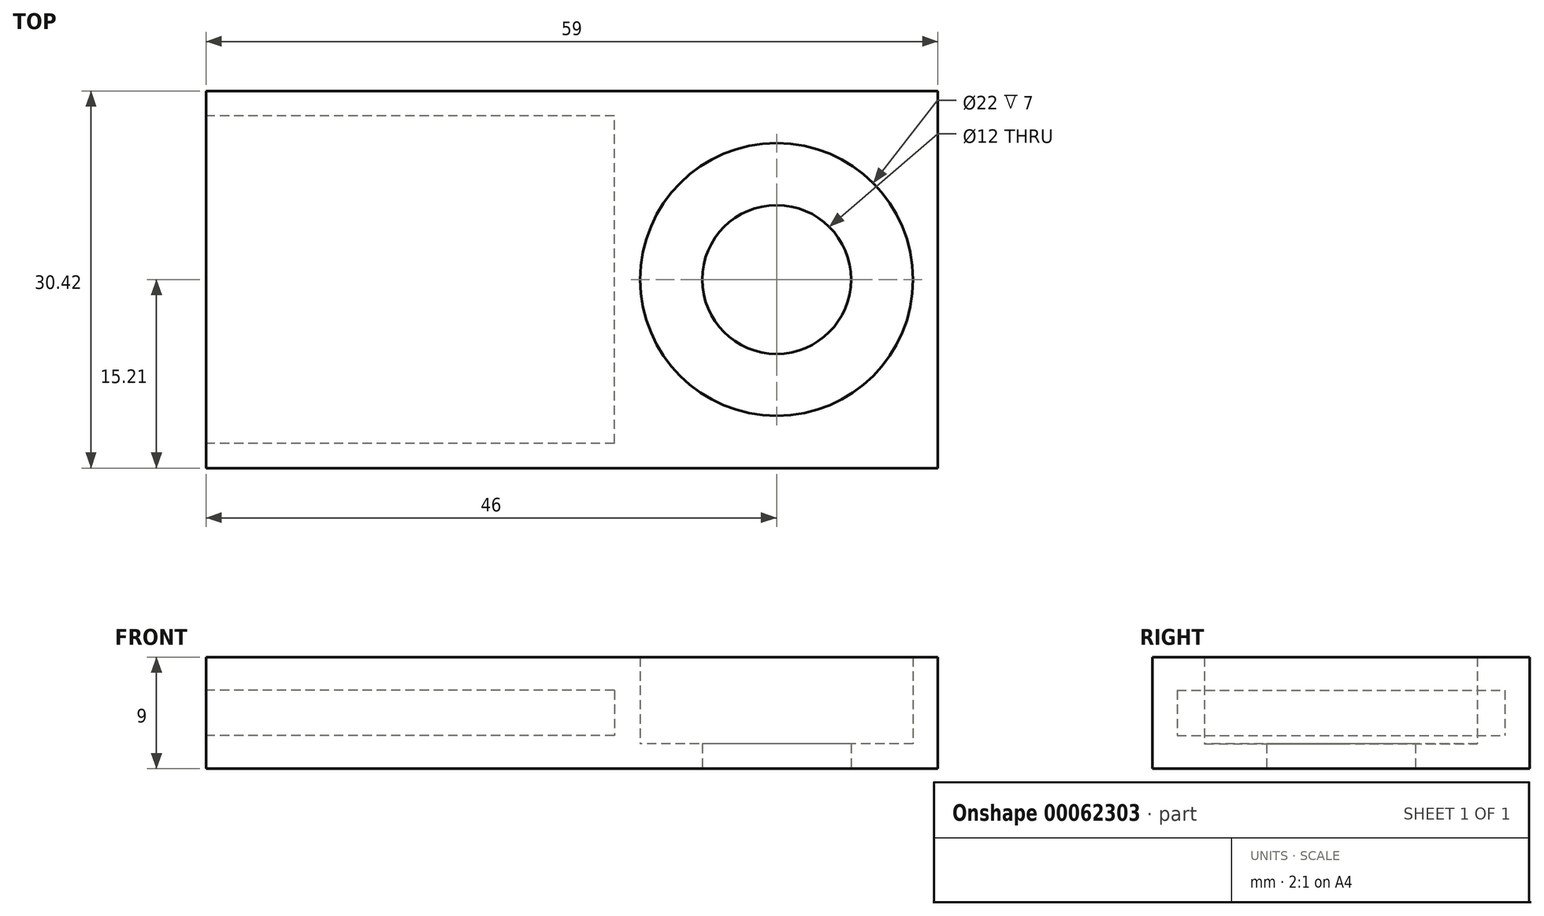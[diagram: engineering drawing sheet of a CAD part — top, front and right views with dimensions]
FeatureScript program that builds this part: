
annotation { "Feature Type Name" : "Feature", "Feature Type Description" : "" }
export const myFeature = defineFeature(function(context is Context, id is Id, definition is map)
    precondition{}
    {
        {
            var Q0;
            Q0=qCreatedBy(makeId("Top.planeOp"),FACE);
            var sketch = newSketch(context, id + "F0", { "sketchPlane" : qUnion([Q0])});
            skCircle(sketch, "E0", {"center": v(0, 0) * mm, "radius": 11 * mm});
            skCircle(sketch, "E1", {"center": v(0, 0) * mm, "radius": 4 * mm, "construction": true});
            skCircle(sketch, "E2.0", {"center": v(0, 0) * mm, "radius": 13 * mm});
            skLineSegment(sketch, "E3.bottom", {"start": v(13, 13.2) * mm, "end": v(-46, 13.2) * mm});
            skLineSegment(sketch, "E3.top", {"start": v(13, -13.2) * mm, "end": v(-46, -13.2) * mm});
            skLineSegment(sketch, "E3.left", {"start": v(13, 13.2) * mm, "end": v(13, -13.2) * mm});
            skLineSegment(sketch, "E3.right", {"start": v(-46, 13.2) * mm, "end": v(-46, -13.2) * mm});
            skLineSegment(sketch, "E4.0", {"start": v(13, 15.2) * mm, "end": v(-46, 15.2) * mm});
            skLineSegment(sketch, "E5.0", {"start": v(13, -15.2) * mm, "end": v(-46, -15.2) * mm});
            skLineSegment(sketch, "E6", {"start": v(13, -15.2) * mm, "end": v(13, -13.2) * mm});
            skLineSegment(sketch, "E7", {"start": v(-46, -15.2) * mm, "end": v(-46, -13.2) * mm});
            skLineSegment(sketch, "E8", {"start": v(-46, 13.2) * mm, "end": v(-46, 15.2) * mm});
            skLineSegment(sketch, "E9", {"start": v(13, 13.2) * mm, "end": v(13, 15.2) * mm});
            skCircle(sketch, "E10.0", {"center": v(0, 0) * mm, "radius": 6 * mm});
            skSolve(sketch);
        }
        {
            var Q0;
            Q0 = qSketchRegion(id + "F0", true);
            extrude(context, id + "F1", {"entities" : qUnion([Q0]), "depth" : 9 * mm});
        }
        {
            var Q0;
            Q0=makeQuery(id+"F0.imprint","IMPRINT",FACE,{"disambiguationData":[TD([[makeQuery(id+"F0.imprint","IMPRINT",EDGE,{"derivedFrom":sQuery(id+"F0.wireOp",EDGE,"E0")}),1.0]])]});
            extrude(context, id + "F2", {"entities" : qUnion([Q0]), "operationType" : NewBodyOperationType.ADD, "depth" : 2 * mm});
        }
        {
            var Q0;
            Q0=makeQuery(id+"F1.opExtrude","SWEPT_FACE",FACE,{"disambiguationData":[OSD([sQuery(id+"F0.wireOp",EDGE,"E3.right"),sQuery(id+"F0.wireOp",EDGE,"E7"),sQuery(id+"F0.wireOp",EDGE,"E8")])]});
            var sketch = newSketch(context, id + "F3", { "sketchPlane" : qUnion([Q0])});
            skLineSegment(sketch, "E11.rect.bottom", {"start": v(13.21, 6.33) * mm, "end": v(-13.21, 6.33) * mm});
            skLineSegment(sketch, "E11.rect.top", {"start": v(13.21, 2.67) * mm, "end": v(-13.21, 2.67) * mm});
            skLineSegment(sketch, "E11.rect.left", {"start": v(13.21, 6.33) * mm, "end": v(13.21, 2.67) * mm});
            skLineSegment(sketch, "E11.rect.right", {"start": v(-13.21, 6.33) * mm, "end": v(-13.21, 2.67) * mm});
            skPoint(sketch, "E11.rect.middle", {"position": v(0, 4.5) * mm});
            skPoint(sketch, "E11.rect.middle.positionSnap0", {"position": v(-15.2, 4.5) * mm});
            skPoint(sketch, "E11.rect.centerSnap0", {"position": v(-15.2, 4.5) * mm});
            skSolve(sketch);
        }
        {
            var Q0;
            Q0=makeQuery(id+"F3.imprint","IMPRINT",FACE,{"disambiguationData":[TD([[makeQuery(id+"F3.imprint","IMPRINT",EDGE,{"derivedFrom":sQuery(id+"F3.wireOp",EDGE,"E11.rect.bottom")}),1.0]])]});
            var Q1;
            Q1=makeQuery(id+"F1.opExtrude","SWEPT_FACE",FACE,{"disambiguationData":[OSD([sQuery(id+"F0.wireOp",EDGE,"E0")])]});
            var Q2;
            Q2=makeQuery(id+"F1.opExtrude","SWEPT_BODY",BODY,{"disambiguationData":[OSD([sQuery(id+"F0.wireOp",EDGE,"E0"),sQuery(id+"F0.wireOp",EDGE,"E3.left"),sQuery(id+"F0.wireOp",EDGE,"E3.right"),sQuery(id+"F0.wireOp",EDGE,"E4.0"),sQuery(id+"F0.wireOp",EDGE,"E5.0"),sQuery(id+"F0.wireOp",EDGE,"E6"),sQuery(id+"F0.wireOp",EDGE,"E7"),sQuery(id+"F0.wireOp",EDGE,"E8"),sQuery(id+"F0.wireOp",EDGE,"E9")])]});
            extrude(context, id + "F4", {"entities" : qUnion([Q0]), "operationType" : NewBodyOperationType.REMOVE, "oppositeDirection" : true, "endBoundEntityFace" : qUnion([Q1]), "endBoundEntityBody" : qUnion([Q2]), "depth" : 32.9 * mm});
        }
    });
